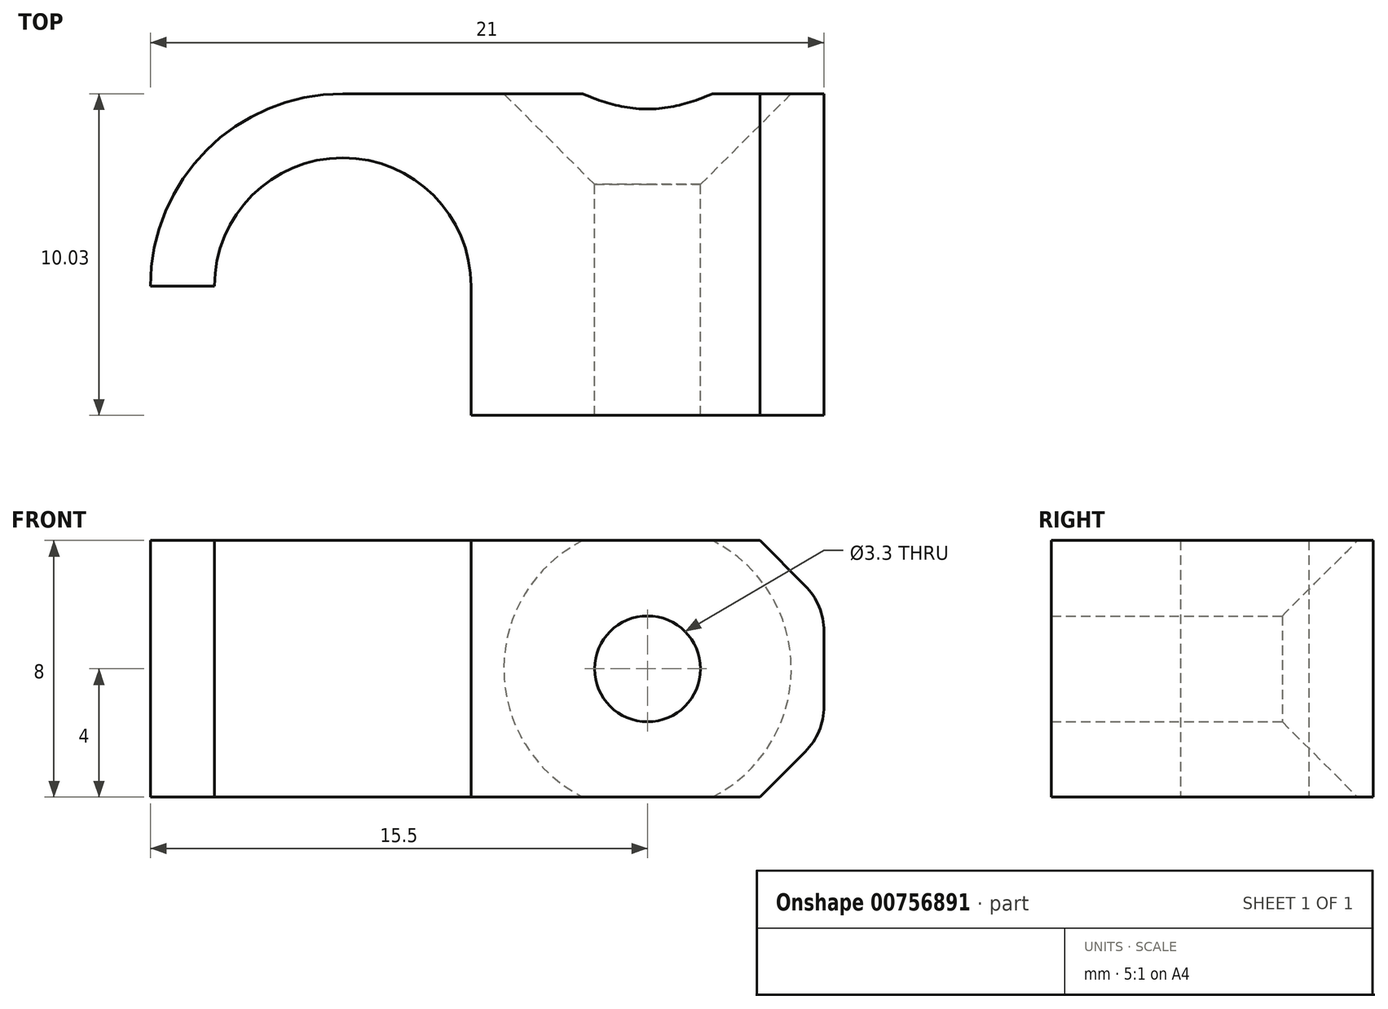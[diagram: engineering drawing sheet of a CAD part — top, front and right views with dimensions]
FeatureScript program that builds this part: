
annotation { "Feature Type Name" : "Feature", "Feature Type Description" : "" }
export const myFeature = defineFeature(function(context is Context, id is Id, definition is map)
    precondition{}
    {
        {
            var Q0;
            Q0=qCreatedBy(makeId("Top.planeOp"),FACE);
            var sketch = newSketch(context, id + "F0", { "sketchPlane" : qUnion([Q0])});
            skArc(sketch, "E0", {"start": v(4, 0) * mm, "mid": v(0, 4) * mm, "end": v(-4, 0) * mm});
            skArc(sketch, "E1.0", {"start": v(0, 6) * mm, "mid": v(-4.24, 4.24) * mm, "end": v(-6, 0) * mm});
            skLineSegment(sketch, "E2", {"start": v(0, 6) * mm, "end": v(15, 6) * mm});
            skLineSegment(sketch, "E3", {"start": v(15, 6) * mm, "end": v(15, -4.03) * mm});
            skLineSegment(sketch, "E4", {"start": v(15, -4.03) * mm, "end": v(4, -4.03) * mm});
            skLineSegment(sketch, "E5", {"start": v(4, 0) * mm, "end": v(4, -4.03) * mm});
            skLineSegment(sketch, "E6", {"start": v(-6, 0) * mm, "end": v(-4, 0) * mm});
            skPoint(sketch, "E7.orphan", {"position": v(0, -4.03) * mm});
            skSolve(sketch);
        }
        {
            var Q0;
            Q0=makeQuery(id+"F0.imprint","IMPRINT",FACE,{"disambiguationData":[TD([[makeQuery(id+"F0.imprint","IMPRINT",EDGE,{"derivedFrom":sQuery(id+"F0.wireOp",EDGE,"E0")}),-1.0]])]});
            extrude(context, id + "F1", {"entities" : qUnion([Q0]), "endBound" : BoundingType.SYMMETRIC, "depth" : 8 * mm, "offsetDistance" : 25 * mm});
        }
        {
            var Q0;
            Q0=makeQuery(id+"F1.opExtrude","SWEPT_FACE",FACE,{"disambiguationData":[OSD([sQuery(id+"F0.wireOp",EDGE,"E2")])]});
            var sketch = newSketch(context, id + "F2", { "sketchPlane" : qUnion([Q0])});
            skLineSegment(sketch, "E8", {"start": v(-15, 4) * mm, "end": v(-4, -4) * mm, "construction": true});
            skPoint(sketch, "E9", {"position": v(-9.5, 0) * mm});
            skSolve(sketch);
        }
        {
            var Q0;
            Q0=sQuery(id+"F2.wireOp",VERTEX,"E9");
            var Q1;
            Q1=makeQuery(id+"F1.opExtrude","SWEPT_BODY",BODY,{"disambiguationData":[OSD([sQuery(id+"F0.wireOp",EDGE,"E0"),sQuery(id+"F0.wireOp",EDGE,"E1.0"),sQuery(id+"F0.wireOp",EDGE,"E2"),sQuery(id+"F0.wireOp",EDGE,"E3"),sQuery(id+"F0.wireOp",EDGE,"E4"),sQuery(id+"F0.wireOp",EDGE,"E5"),sQuery(id+"F0.wireOp",EDGE,"E6")])]});
            hole(context, id + "F3", {"style" : HoleStyle.C_SINK, "endStyle" : HoleEndStyle.THROUGH, "standardTappedOrClearance" : lookupTablePath({ "standard" : "ISO", "engagement" : "75%", "pitch" : "0.7 mm", "size" : "M4", "type" : "Tapped" }), "standardBlindInLast" : lookupTablePath({ "standard" : "ISO", "engagement" : "75%", "pitch" : "0.7 mm", "size" : "M4", "type" : "Tapped" }), "holeDiameter" : 3.3 * mm, "cSinkDiameter" : 8.96 * mm, "cSinkAngle" : 90 * degree, "majorDiameter" : 4 * mm, "showTappedDepth" : true, "isTappedThrough" : true, "tappedDepth" : 12 * mm, "tapClearance" : 3, "locations" : qUnion([Q0]), "scope" : qUnion([Q1])});
        }
        {
            var Q0;
            Q0=makeQuery(id+"F1.opExtrude","CAP_EDGE",EDGE,{"disambiguationData":[OSD([sQuery(id+"F0.wireOp",EDGE,"E3")])],"isStart":true});
            var Q1;
            Q1=makeQuery(id+"F1.opExtrude","CAP_EDGE",EDGE,{"disambiguationData":[OSD([sQuery(id+"F0.wireOp",EDGE,"E3")])],"isStart":false});
            chamfer(context, id + "F4", {"entities" : qUnion([Q0, Q1]), "width" : 2 * mm, "tangentPropagation" : true});
        }
        {
            var Q0;
            {var subQ0=sQuery(id+"F0.wireOp",EDGE,"E3");Q0=makeQuery(id+"F4.opChamfer","BLEND_EDGE",EDGE,{"blendedFrom":[makeQuery(id+"F1.opExtrude","CAP_EDGE",EDGE,{"disambiguationData":[OSD([subQ0])],"isStart":true}),makeQuery(id+"F1.opExtrude","SWEPT_FACE",FACE,{"disambiguationData":[OSD([subQ0])]})],"blendedInto":[makeQuery(id+"F1.opExtrude","SWEPT_FACE",FACE,{"disambiguationData":[OSD([subQ0])]})]});}
            var Q1;
            {var subQ0=sQuery(id+"F0.wireOp",EDGE,"E3");Q1=makeQuery(id+"F4.opChamfer","BLEND_EDGE",EDGE,{"blendedFrom":[makeQuery(id+"F1.opExtrude","CAP_EDGE",EDGE,{"disambiguationData":[OSD([subQ0])],"isStart":false}),makeQuery(id+"F1.opExtrude","SWEPT_FACE",FACE,{"disambiguationData":[OSD([subQ0])]})],"blendedInto":[makeQuery(id+"F1.opExtrude","SWEPT_FACE",FACE,{"disambiguationData":[OSD([subQ0])]})]});}
            fillet(context, id + "F5", {"entities" : qUnion([Q0, Q1]), "radius" : 2 * mm, "tangentPropagation" : true, "allowEdgeOverflow" : false});
        }
    });
